# Revit family: SW12 AART
name_source: partatom
category: Detail Items
units: mm (PartAtom-declared; Revit-internal decimal feet)

## family parameters
Rotate with component = No
Section Shape = Not Defined
Shared = No

## types (5) — shared parameters
URL = www.superwood.dk

## per-type parameters (varying)
| type | Højde | Large | Medium | Small | Small (uden spor) |
| SW12 AART 4" SMALL - 27x95mm | 80 mm  [stored 0.262467 ft] | No | No | No | Yes |
| SW12 AART 4" MEDIUM - 27x95mm | 80 mm  [stored 0.262467 ft] | No | Yes | No | No |
| SW12 AART 6" SMALL - 27x145mm | 80 mm  [stored 0.262467 ft] | No | No | Yes | No |
| SW12 AART 6" MEDIUM - 27x145mm | 130 mm  [stored 0.426509 ft] | No | Yes | No | No |
| SW12 AART 6" LARGE - 27x145mm | 80 mm  [stored 0.262467 ft] | Yes | No | No | No |

note: [stored X ft] marks values corroborated as IEEE doubles in the binary element streams (Revit-internal decimal feet)

## geometry (parser evidence)
native form markers: Sweep x8
no freeform markers — native parametric forms only
